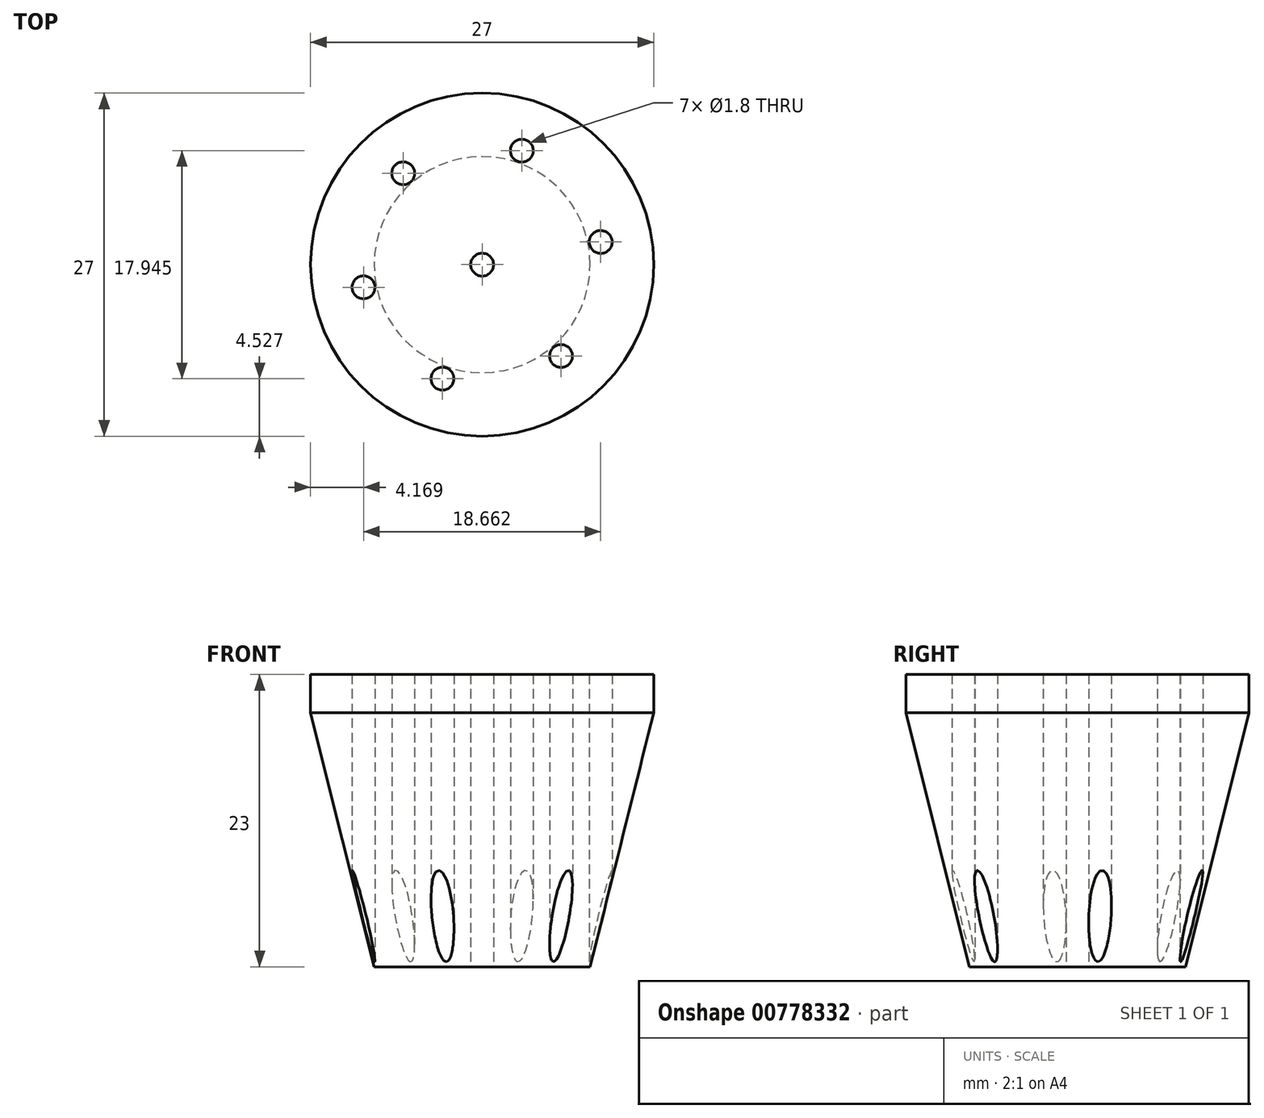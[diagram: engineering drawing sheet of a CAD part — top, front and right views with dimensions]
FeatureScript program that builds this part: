
annotation { "Feature Type Name" : "Feature", "Feature Type Description" : "" }
export const myFeature = defineFeature(function(context is Context, id is Id, definition is map)
    precondition{}
    {
        {
            var Q0;
            Q0=qCreatedBy(makeId("Top.planeOp"),FACE);
            var sketch = newSketch(context, id + "F0", { "sketchPlane" : qUnion([Q0])});
            skCircle(sketch, "E0.cCircle", {"center": v(0, 0) * mm, "radius": 9.5 * mm, "construction": true});
            skLineSegment(sketch, "E0.0", {"start": v(-3.12, -8.97) * mm, "end": v(-9.33, -1.78) * mm, "construction": true});
            skLineSegment(sketch, "E0.1", {"start": v(-9.33, -1.78) * mm, "end": v(-6.2, 7.19) * mm, "construction": true});
            skLineSegment(sketch, "E0.2", {"start": v(-6.2, 7.19) * mm, "end": v(3.12, 8.97) * mm, "construction": true});
            skLineSegment(sketch, "E0.3", {"start": v(3.12, 8.97) * mm, "end": v(9.33, 1.78) * mm, "construction": true});
            skLineSegment(sketch, "E0.4", {"start": v(9.33, 1.78) * mm, "end": v(6.2, -7.19) * mm, "construction": true});
            skLineSegment(sketch, "E0.5", {"start": v(6.2, -7.19) * mm, "end": v(-3.12, -8.97) * mm, "construction": true});
            skCircle(sketch, "E1", {"center": v(-6.2, 7.19) * mm, "radius": 0.9 * mm});
            skCircle(sketch, "E2", {"center": v(3.12, 8.97) * mm, "radius": 0.9 * mm});
            skCircle(sketch, "E3", {"center": v(9.33, 1.78) * mm, "radius": 0.9 * mm});
            skCircle(sketch, "E4", {"center": v(6.2, -7.19) * mm, "radius": 0.9 * mm});
            skCircle(sketch, "E5", {"center": v(-3.12, -8.97) * mm, "radius": 0.9 * mm});
            skCircle(sketch, "E6", {"center": v(-9.33, -1.78) * mm, "radius": 0.9 * mm});
            skCircle(sketch, "E7", {"center": v(0, 0) * mm, "radius": 0.9 * mm});
            skCircle(sketch, "E8", {"center": v(0, 0) * mm, "radius": 13.5 * mm});
            skSolve(sketch);
        }
        {
            var Q0;
            Q0 = qSketchRegion(id + "F0", true);
            extrude(context, id + "F1", {"entities" : qUnion([Q0]), "depth" : 23 * mm, "offsetDistance" : 25 * mm});
        }
        {
            var Q0;
            Q0=makeQuery(id+"F1.opExtrude","CAP_EDGE",EDGE,{"disambiguationData":[OSD([sQuery(id+"F0.wireOp",EDGE,"E8")])],"isStart":true});
            chamfer(context, id + "F2", {"entities" : qUnion([Q0]), "chamferType" : ChamferType.TWO_OFFSETS, "width1" : 20 * mm, "oppositeDirection" : false, "width2" : 5 * mm, "tangentPropagation" : true});
        }
    });
